# Revit family: SEMR_End
name_source: partatom
category: Lighting Fixtures
revit_build: Autodesk Revit 2014 (Build: 20130308_1515(x64)
units: mm (PartAtom-declared; Revit-internal decimal feet)

## types (1)
- SEMR
    Apparent Load = 4 VA
    Application = The Sempra® MR Series are a set of compact, low-profile Master/
Remote exit sign featuring cast aluminum construction. It allows for
easy installation and has energy saving, long-life LED lamps.
    Certification = UL 924 Listed
NFPA 101 Life Safety Code
CEC T20 Compliant
    Default Elevation = 48.000"
    Description = A nickel-cadmium battery is supplied with master exits and comes with a solid state constant current type charger. Transfer to emergency
operation is completely automatic upon failure of utility AC voltage. Units also have a built-in protection for transformer isolation, surge,
transient and low voltage disconnect. Emergency operation shall be provided for a minimum of 90 minutes. Full battery recharge occurs
in compliance with UL 924 specifications. A universal 120/277 VAC, 60Hz input transformer, test switch and long life AC pilot light are all
provided standard. Exit signs must comply with all UL 924 and NFPA 101 Life Safety Code requirement
    Double Face = Yes
    End = End : C1
    Features = High-strength cast aluminum construction
• Compact, low-profile style
• Red and Green letters
• Break out chevron directional arrows
• Wide range of options including vandal/tamper-proof
    Finish = Hubbell - White
    Glass = Hubbell - light Glass
    Holder Material = Hubbell - Steel
    Lamp = LED Lamp
    Lens = Hubbell - Green Glass
    Load Classification = Lighting
    Manufacturer = DUAL-LITE
    Model = SEMR
    Product Documentation Link = https://hubbellcdn.com
    Product Page URL = https://www.hubbell.com
    Single Face = Yes
    Type Comments = Exit Light
    URL = https://www.hubbell.com
    Wall Plate Material = Hubbell - Black
    Warranty = Fixture: 5 Years Full; Battery: 2 Years Full, 8 Years Pro-Rata
    Wattage Comments = 3.72 W
    Watts = 4 W

## geometry (parser evidence)
native form markers: Blend x6, Sweep x4
no freeform markers — native parametric forms only
